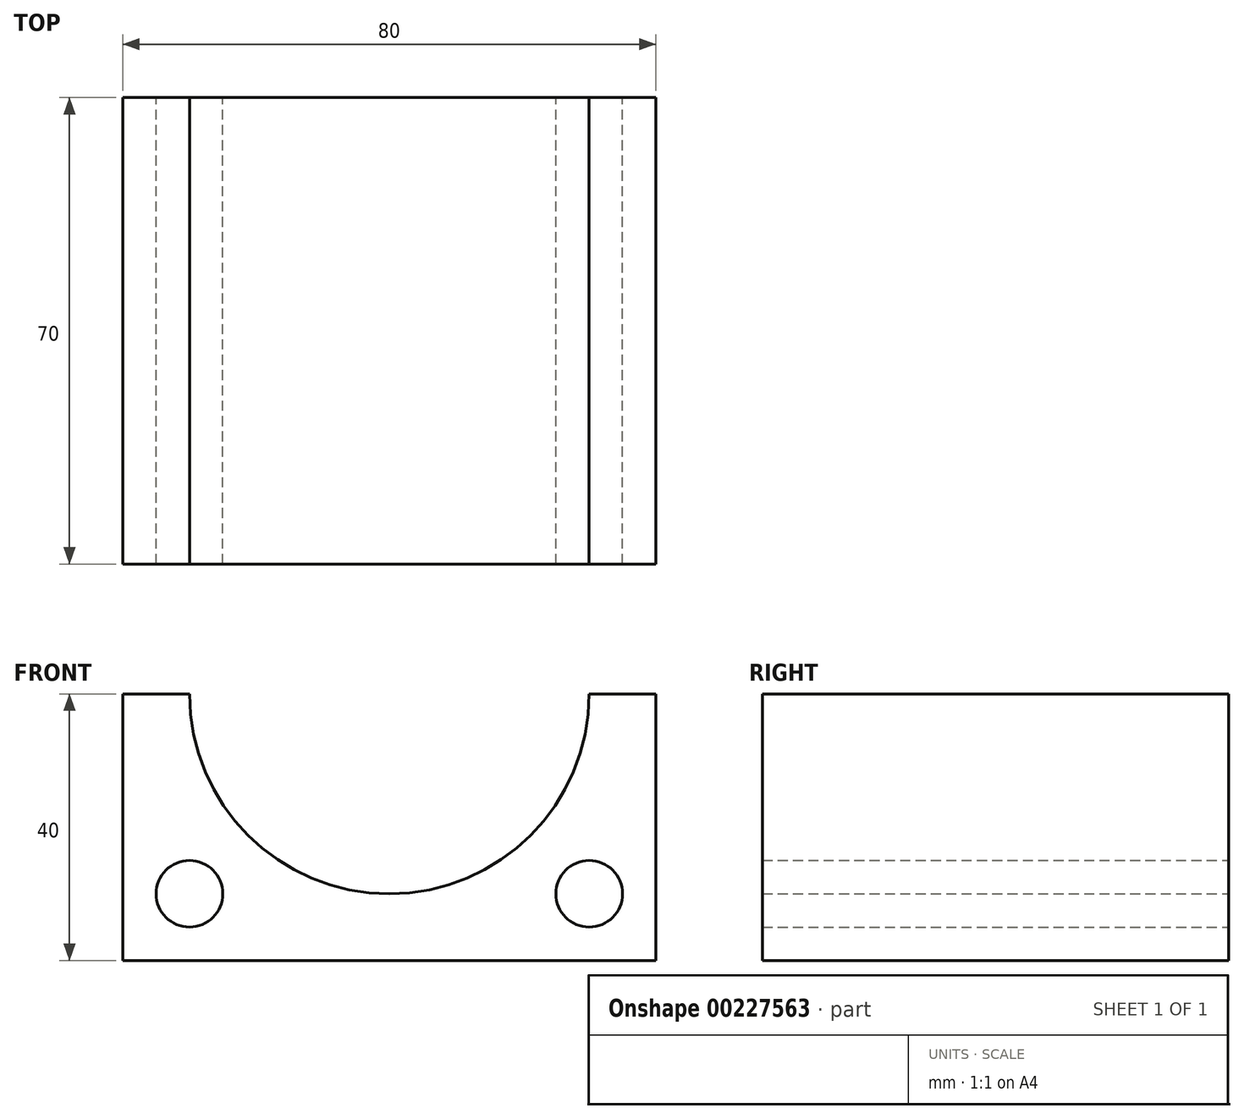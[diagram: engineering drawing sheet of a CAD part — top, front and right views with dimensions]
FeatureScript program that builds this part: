
annotation { "Feature Type Name" : "Feature", "Feature Type Description" : "" }
export const myFeature = defineFeature(function(context is Context, id is Id, definition is map)
    precondition{}
    {
        {
            var Q0;
            Q0=qCreatedBy(makeId("Front.planeOp"),FACE);
            var sketch = newSketch(context, id + "F0", { "sketchPlane" : qUnion([Q0])});
            skLineSegment(sketch, "E0", {"start": v(0, 40) * mm, "end": v(0, 0) * mm});
            skLineSegment(sketch, "E1", {"start": v(0, 0) * mm, "end": v(80, 0) * mm});
            skArc(sketch, "E2", {"start": v(10, 40) * mm, "mid": v(40, 10) * mm, "end": v(70, 40) * mm});
            skLineSegment(sketch, "E3", {"start": v(0, 40) * mm, "end": v(10, 40) * mm});
            skLineSegment(sketch, "E4", {"start": v(80, 40) * mm, "end": v(70, 40) * mm});
            skCircle(sketch, "E5", {"center": v(10, 10) * mm, "radius": 5 * mm});
            skCircle(sketch, "E6", {"center": v(70, 10) * mm, "radius": 5 * mm});
            skLineSegment(sketch, "E7", {"start": v(0, 25) * mm, "end": v(14.02, 25) * mm});
            skLineSegment(sketch, "E8", {"start": v(40, 10) * mm, "end": v(40, 0) * mm});
            skLineSegment(sketch, "E9", {"start": v(80, 40) * mm, "end": v(80, 0) * mm});
            skSolve(sketch);
        }
        {
            var Q0;
            {var subQ0=sQuery(id+"F0.wireOp",EDGE,"E3");Q0=makeQuery(id+"F0.imprint","IMPRINT",FACE,{"disambiguationData":[TD([[makeQuery(id+"F0.imprint","IMPRINT",EDGE,{"derivedFrom":subQ0}),-1.0]])]});}
            var Q1;
            {var subQ3=sQuery(id+"F0.wireOp",EDGE,"E4");Q1=makeQuery(id+"F0.imprint","IMPRINT",FACE,{"disambiguationData":[TD([[makeQuery(id+"F0.imprint","IMPRINT",EDGE,{"derivedFrom":subQ3}),1.0]])]});}
            extrude(context, id + "F1", {"entities" : qUnion([Q0, Q1]), "depth" : 30 * mm});
        }
        {
            var Q0;
            Q0=makeQuery(id+"F0.imprint","IMPRINT",FACE,{"disambiguationData":[TD([[makeQuery(id+"F0.imprint","IMPRINT",EDGE,{"derivedFrom":sQuery(id+"F0.wireOp",EDGE,"E5")}),-1.0]])]});
            extrude(context, id + "F2", {"entities" : qUnion([Q0]), "operationType" : NewBodyOperationType.ADD, "depth" : 40 * mm});
        }
        {
            var Q0;
            Q0 = qSketchRegion(id + "F0", true);
            extrude(context, id + "F3", {"entities" : qUnion([Q0]), "depth" : 30 * mm});
        }
        {
            var Q0;
            Q0=makeQuery(id+"F3.opExtrude","CAP_FACE",FACE,{"disambiguationData":[OSD([sQuery(id+"F0.wireOp",EDGE,"E0"),sQuery(id+"F0.wireOp",EDGE,"E1"),sQuery(id+"F0.wireOp",EDGE,"E2"),sQuery(id+"F0.wireOp",EDGE,"E5"),sQuery(id+"F0.wireOp",EDGE,"E7"),sQuery(id+"F0.wireOp",EDGE,"E8")])],"isStart":false});
            extrude(context, id + "F4", {"entities" : qUnion([Q0]), "operationType" : NewBodyOperationType.ADD, "depth" : 40 * mm});
        }
    });
